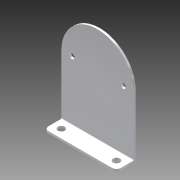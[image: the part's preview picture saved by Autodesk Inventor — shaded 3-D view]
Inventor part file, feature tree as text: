
AUTODESK INVENTOR PART (.ipt)
format: ipt  version: 2016 SP1 (Build 200210100, 210)  size: 115,712 bytes
history: native  units: in
note: dims shown in document units (in); Inventor stores cm internally (conversion verified against a paired STEP export)
features: fillet x3, hole x3, sketch x3, extrude x2, reference x2
ambient origin geometry x8: Origin, YZ Plane, XZ Plane, XY Plane, X Axis, Y Axis, Z Axis, Center Point
bodies: Solid1 (feature_tree)
feature tree (13):
  extrude  "Extrusion1"  Depth=0.0625in
  extrude  "Extrusion2"  Depth=0.125in
  fillet  "Fillet1"  Radius=0.0312in
  hole  "Hole1"  [1 undecoded]
  fillet  "Fillet2"  Radius=0.75in
  hole  "Hole2"  [1 undecoded]
  hole  "Hole3"  [1 undecoded]
  fillet  "Fillet3"  [1 undecoded]
  sketch  "Sketch1"  dims[d0=0.0625in d1=0.0in d2=0.0625in]
  reference  "Reference1"
  sketch  "Sketch2"  dims[d3=0.5in d4=0.0in d5=0.125in]
  sketch  "Sketch3"  dims[d6=0.25in d16=0.25in d8=0.201in d9=0.75in d10=0.385in d11=0.25in d12=0.5635in d13=1.0in d14=0.8108in d15=0.0312in d17=0.25in d18=0.25in d19=0.201in d20=0.75in d21=0.385in d22=0.25in d23=0.5635in d24=1.0in d25=0.8108in d26=0.75in d27=0.75in d28=0.15in d29=0.75in d30=0.385in d31=0.25in d32=0.5635in d33=1.0in d34=0.8108in d35=0.125in]
  reference  "Reference3"
note: 4 required parameter values undecoded (feature->parameter linkage not recoverable at this tier; creation-order binding heuristic only, values carry confidence <= 0.55)
